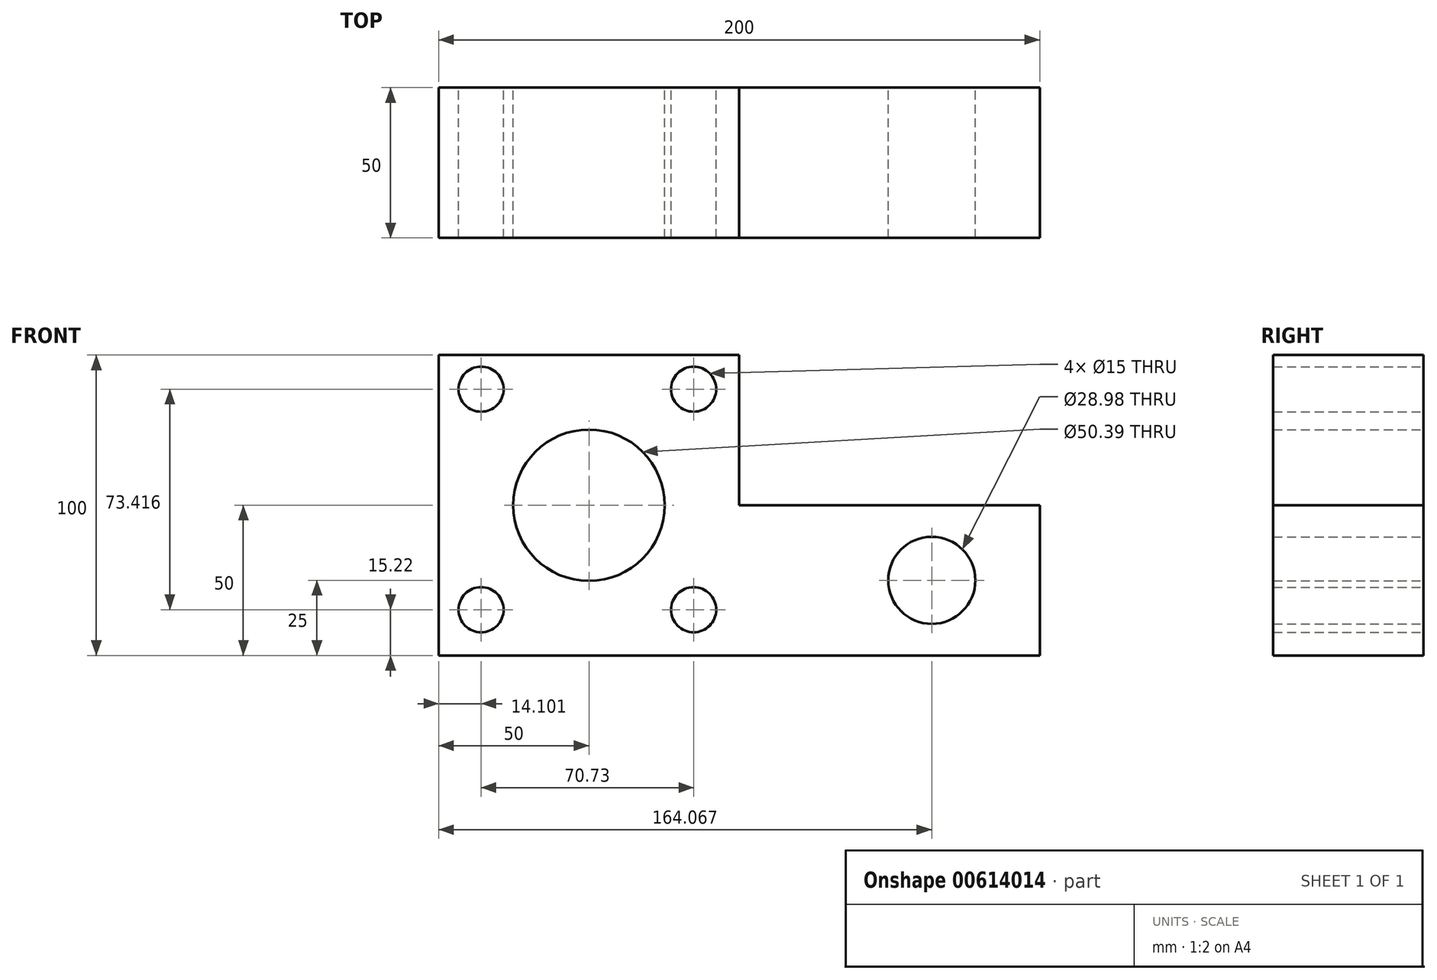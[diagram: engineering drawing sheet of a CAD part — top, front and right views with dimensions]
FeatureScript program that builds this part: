
annotation { "Feature Type Name" : "Feature", "Feature Type Description" : "" }
export const myFeature = defineFeature(function(context is Context, id is Id, definition is map)
    precondition{}
    {
        {
            var Q0;
            Q0=qCreatedBy(makeId("Front.planeOp"),FACE);
            var sketch = newSketch(context, id + "F0", { "sketchPlane" : qUnion([Q0])});
            skLineSegment(sketch, "E0", {"start": v(0, 0) * mm, "end": v(200, 0) * mm});
            skLineSegment(sketch, "E1", {"start": v(200, 0) * mm, "end": v(200, 50) * mm});
            skLineSegment(sketch, "E2", {"start": v(200, 50) * mm, "end": v(100, 50) * mm});
            skLineSegment(sketch, "E3", {"start": v(100, 50) * mm, "end": v(100, 100) * mm});
            skLineSegment(sketch, "E4", {"start": v(100, 100) * mm, "end": v(0, 100) * mm});
            skLineSegment(sketch, "E5", {"start": v(0, 100) * mm, "end": v(0, 0) * mm});
            skCircle(sketch, "E6", {"center": v(164.07, 25) * mm, "radius": 14.49 * mm});
            skPoint(sketch, "E6.centerSnap0", {"position": v(200, 25) * mm});
            skCircle(sketch, "E7", {"center": v(50, 50) * mm, "radius": 25.2 * mm});
            skPoint(sketch, "E7.centerSnap0", {"position": v(50, 100) * mm});
            skPoint(sketch, "E7.centerSnap1", {"position": v(0, 50) * mm});
            skCircle(sketch, "E8", {"center": v(84.83, 88.64) * mm, "radius": 7.5 * mm});
            skCircle(sketch, "E9", {"center": v(84.83, 15.22) * mm, "radius": 7.5 * mm});
            skCircle(sketch, "E10", {"center": v(14.1, 15.22) * mm, "radius": 7.5 * mm});
            skCircle(sketch, "E11", {"center": v(14.1, 88.64) * mm, "radius": 7.5 * mm});
            skSolve(sketch);
        }
        {
            var Q0;
            Q0 = qSketchRegion(id + "F0", true);
            extrude(context, id + "F1", {"entities" : qUnion([Q0]), "depth" : 50 * mm, "offsetDistance" : 25 * mm});
        }
    });
